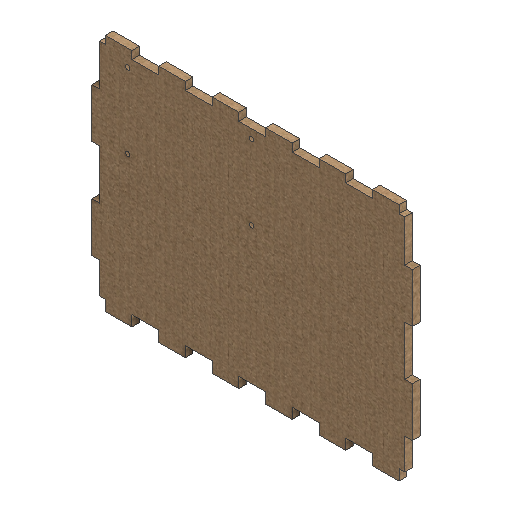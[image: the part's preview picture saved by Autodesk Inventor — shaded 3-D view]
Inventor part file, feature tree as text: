
AUTODESK INVENTOR PART (.ipt)
format: ipt  version: 2025.2 (Build 292293000, 293)  size: 452,608 bytes
history: native  units: mm
features: sketch x10, extrude x5, projected_geometry x2, hole x1
ambient origin geometry x8: Origin, YZ Plane, XZ Plane, XY Plane, X Axis, Y Axis, Z Axis, Center Point
bodies: Solid1 (feature_tree)
feature tree (18):
  extrude  "Extrusion1"  Depth=210.0mm
  hole  "Hole2"  [1 undecoded]
  extrude  "Extrusion2"  Depth=23.5mm
  extrude  "Extrusion3"  Depth=10.0mm TaperAngle=0.0deg
  extrude  "Extrusion4"  Depth=32.46mm
  extrude  "Extrusion5"  Depth=32.26mm
  sketch  "Sketch1"  dims[d0=210.0mm d1=161.8mm]
  sketch  "Sketch3"  dims[d11=3.0mm d12=6.0mm d13=4.0mm d14=2.0mm d15=90.0deg d16=8.0mm d17=20.594885mm d20=49.0mm]
  sketch  "Sketch4"  dims[d23=11.0mm d35=10.0mm d36=0.0mm]
  projected_geometry  "Projected Loop1"
  sketch  "Sketch5"  dims[d39=5.1mm d40=32.26mm]
  sketch  "Sketch Rectangular Pattern2"  dims[d2=5.0mm d3=0.0mm]
  sketch  "Sketch Rectangular Pattern3"  dims[d21=81.0mm d22=23.5mm]
  sketch  "Sketch7"  dims[d43=210.0mm]
  sketch  "Sketch Rectangular Pattern4"  dims[d37=32.46mm d38=161.8mm]
  sketch  "Sketch Rectangular Pattern5"  dims[d41=10.0mm d42=0.0mm]
  sketch  "Sketch8"  dims[d44=17.6mm d45=5.1mm d46=40.0mm d48=35.0mm d49=10.0mm d51=10.0mm d53=40.0mm d55=35.0mm d56=10.0mm d58=10.0mm d61=40.0mm d63=10.0mm d65=40.0mm d67=10.0mm d68=210.0mm d69=17.6mm d70=12.0mm d71=35.0mm d72=35.0mm d73=10.0mm d74=10.0mm d75=10.0mm d76=0.0mm d77=5.0mm d78=10.0mm d79=0.0mm]
  projected_geometry  "Projected Loop2"
note: 1 required parameter value undecoded (feature->parameter linkage not recoverable at this tier; creation-order binding heuristic only, values carry confidence <= 0.55)
